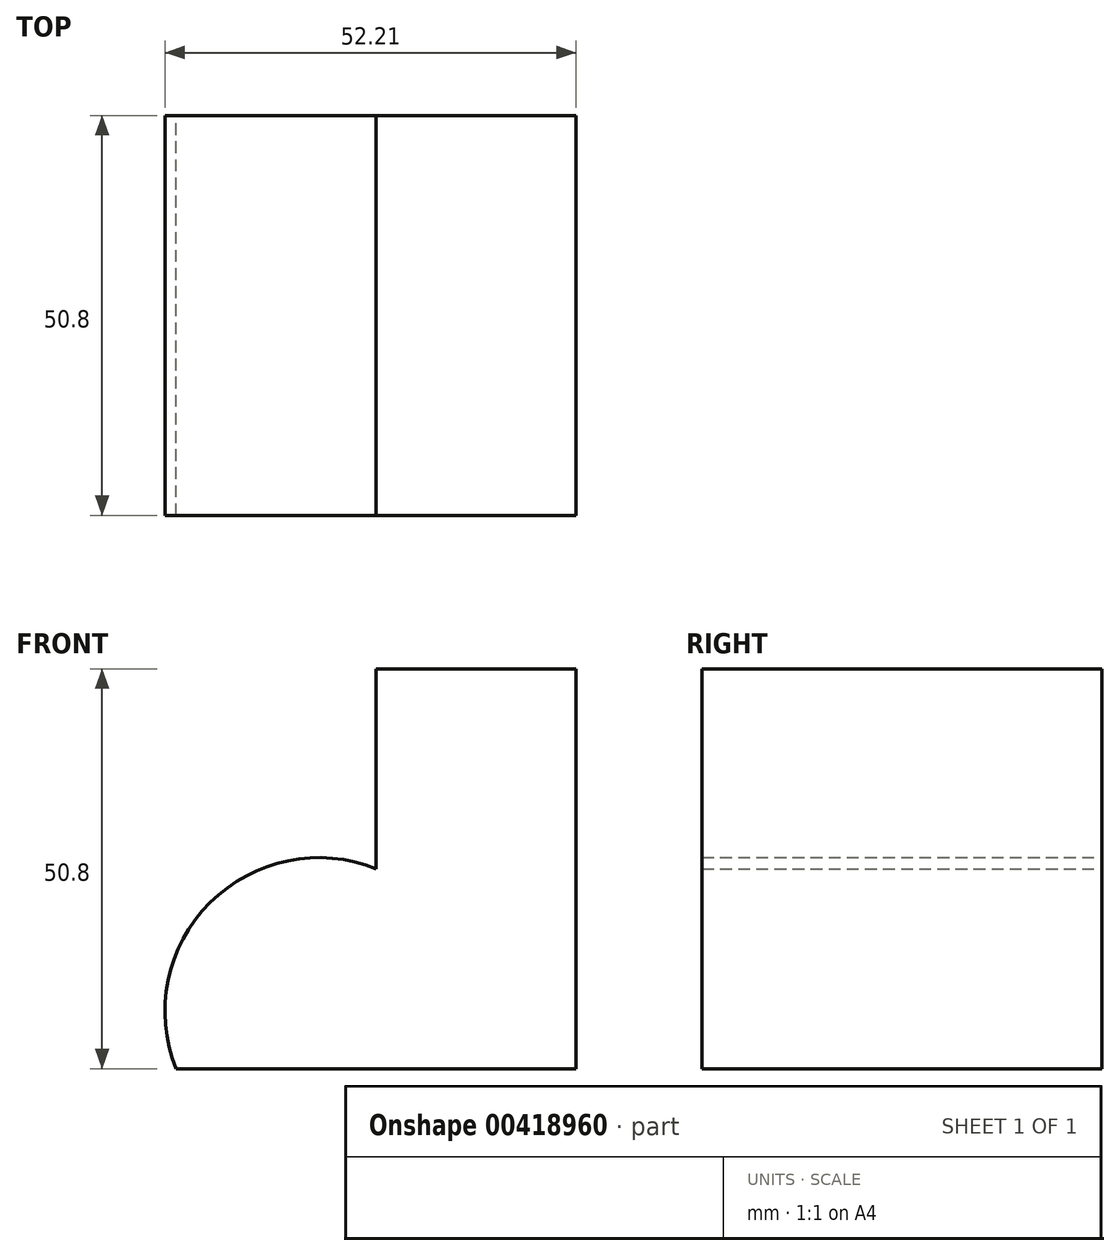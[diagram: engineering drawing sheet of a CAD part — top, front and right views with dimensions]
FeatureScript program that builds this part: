
annotation { "Feature Type Name" : "Feature", "Feature Type Description" : "" }
export const myFeature = defineFeature(function(context is Context, id is Id, definition is map)
    precondition{}
    {
        {
            var Q0;
            Q0=qCreatedBy(makeId("Front.planeOp"),FACE);
            var sketch = newSketch(context, id + "F0", { "sketchPlane" : qUnion([Q0])});
            skLineSegment(sketch, "E0", {"start": v(0, 50.8) * mm, "end": v(0, 0) * mm});
            skLineSegment(sketch, "E1", {"start": v(0, 0) * mm, "end": v(0, 50.8) * mm});
            skLineSegment(sketch, "E2", {"start": v(0, 50.8) * mm, "end": v(-25.4, 50.8) * mm});
            skLineSegment(sketch, "E3", {"start": v(-25.4, 50.8) * mm, "end": v(-25.4, 25.4) * mm});
            skLineSegment(sketch, "E4", {"start": v(0, 0) * mm, "end": v(-50.8, 0) * mm});
            skArc(sketch, "E5", {"start": v(-25.4, 25.4) * mm, "mid": v(-46.5, 21.1) * mm, "end": v(-50.8, 0) * mm});
            skSolve(sketch);
        }
        {
            var Q0;
            Q0 = qSketchRegion(id + "F0", true);
            extrude(context, id + "F1", {"entities" : qUnion([Q0]), "depth" : 50.8 * mm});
        }
    });
